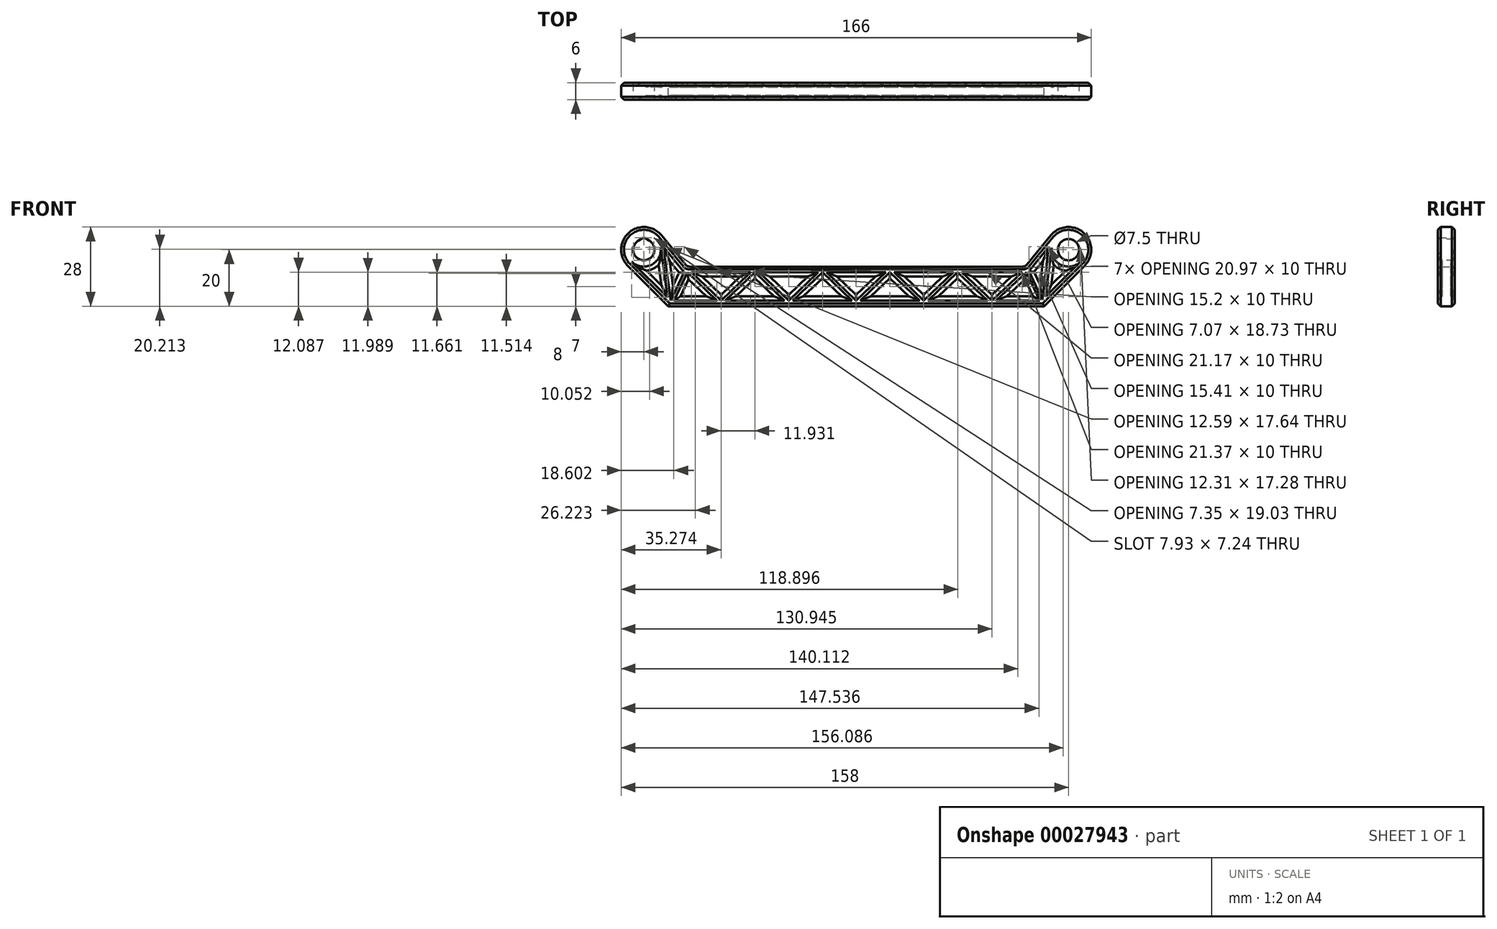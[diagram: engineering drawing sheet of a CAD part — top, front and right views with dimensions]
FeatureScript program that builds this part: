
annotation { "Feature Type Name" : "Feature", "Feature Type Description" : "" }
export const myFeature = defineFeature(function(context is Context, id is Id, definition is map)
    precondition{}
    {
        {
            var Q0;
            Q0=qCreatedBy(makeId("Front.planeOp"),FACE);
            var sketch = newSketch(context, id + "F0", { "sketchPlane" : qUnion([Q0])});
            skArc(sketch, "E0", {"start": v(-68.82, 25.08) * mm, "mid": v(-80.38, 25.92) * mm, "end": v(-80.66, 14.34) * mm});
            skArc(sketch, "E1", {"start": v(80.66, 14.34) * mm, "mid": v(80.38, 25.92) * mm, "end": v(68.82, 25.08) * mm});
            skLineSegment(sketch, "E2", {"start": v(-80.66, 14.34) * mm, "end": v(-66.31, 0) * mm});
            skLineSegment(sketch, "E3", {"start": v(66.31, 0) * mm, "end": v(80.66, 14.34) * mm});
            skLineSegment(sketch, "E4", {"start": v(68.82, 25.08) * mm, "end": v(59.7, 14) * mm});
            skLineSegment(sketch, "E5", {"start": v(59.7, 14) * mm, "end": v(-59.7, 14) * mm});
            skLineSegment(sketch, "E6", {"start": v(-68.82, 25.08) * mm, "end": v(-59.7, 14) * mm});
            skLineSegment(sketch, "E7", {"start": v(-66.31, 0) * mm, "end": v(66.31, 0) * mm});
            skLineSegment(sketch, "E8", {"start": v(59.7, 14) * mm, "end": v(59.7, 0) * mm, "construction": true});
            skLineSegment(sketch, "E9", {"start": v(66.31, 0) * mm, "end": v(55.5, 8.9) * mm, "construction": true});
            skSolve(sketch);
        }
        {
            var Q0;
            Q0 = qSketchRegion(id + "F0", true);
            extrude(context, id + "F1", {"entities" : qUnion([Q0]), "endBound" : BoundingType.SYMMETRIC, "depth" : 6 * mm});
        }
        {
            var Q0;
            Q0=makeQuery(id+"F1.opExtrude","CAP_FACE",FACE,{"disambiguationData":[OSD([sQuery(id+"F0.wireOp",EDGE,"E0"),sQuery(id+"F0.wireOp",EDGE,"E1"),sQuery(id+"F0.wireOp",EDGE,"E2"),sQuery(id+"F0.wireOp",EDGE,"E3"),sQuery(id+"F0.wireOp",EDGE,"E4"),sQuery(id+"F0.wireOp",EDGE,"E5"),sQuery(id+"F0.wireOp",EDGE,"E6"),sQuery(id+"F0.wireOp",EDGE,"E7")])],"isStart":false});
            var sketch = newSketch(context, id + "F2", { "sketchPlane" : qUnion([Q0])});
            skLineSegment(sketch, "E10", {"start": v(-10.48, 12) * mm, "end": v(10.48, 12) * mm});
            skLineSegment(sketch, "E11", {"start": v(10.48, 12) * mm, "end": v(0, 2) * mm});
            skLineSegment(sketch, "E12", {"start": v(0, 2) * mm, "end": v(-10.48, 12) * mm});
            skLineSegment(sketch, "E13", {"start": v(-1.45, 2) * mm, "end": v(-11.93, 12) * mm});
            skLineSegment(sketch, "E14", {"start": v(-11.93, 12) * mm, "end": v(-22.41, 2) * mm});
            skLineSegment(sketch, "E15", {"start": v(-22.41, 2) * mm, "end": v(-1.45, 2) * mm});
            skLineSegment(sketch, "E16", {"start": v(1.45, 2) * mm, "end": v(11.93, 12) * mm});
            skLineSegment(sketch, "E17", {"start": v(11.93, 12) * mm, "end": v(22.41, 2) * mm});
            skLineSegment(sketch, "E18", {"start": v(22.41, 2) * mm, "end": v(1.45, 2) * mm});
            skLineSegment(sketch, "E19", {"start": v(13.38, 12) * mm, "end": v(23.86, 2) * mm});
            skLineSegment(sketch, "E20", {"start": v(13.38, 12) * mm, "end": v(34.35, 12) * mm});
            skLineSegment(sketch, "E21", {"start": v(34.35, 12) * mm, "end": v(23.86, 2) * mm});
            skLineSegment(sketch, "E22", {"start": v(-13.38, 12) * mm, "end": v(-23.86, 2) * mm});
            skLineSegment(sketch, "E23", {"start": v(-23.86, 2) * mm, "end": v(-34.35, 12) * mm});
            skLineSegment(sketch, "E24", {"start": v(-34.35, 12) * mm, "end": v(-13.38, 12) * mm});
            skLineSegment(sketch, "E25", {"start": v(49.4, 2) * mm, "end": v(60.1, 12) * mm});
            skLineSegment(sketch, "E26", {"start": v(60.1, 12) * mm, "end": v(64.82, 2) * mm});
            skLineSegment(sketch, "E27", {"start": v(64.82, 2) * mm, "end": v(49.4, 2) * mm});
            skLineSegment(sketch, "E28", {"start": v(-49.17, 2) * mm, "end": v(-59.66, 12) * mm});
            skLineSegment(sketch, "E29", {"start": v(-59.66, 12) * mm, "end": v(-64.38, 2) * mm});
            skLineSegment(sketch, "E30", {"start": v(-64.38, 2) * mm, "end": v(-49.17, 2) * mm});
            skLineSegment(sketch, "E31", {"start": v(59.7, 14) * mm, "end": v(66.31, 0) * mm, "construction": true});
            skLineSegment(sketch, "E32", {"start": v(-60.72, 12.09) * mm, "end": v(-65.49, 2) * mm});
            skLineSegment(sketch, "E33", {"start": v(-66.65, 3.17) * mm, "end": v(-79.24, 15.76) * mm});
            skLineSegment(sketch, "E34", {"start": v(-68.08, 21.03) * mm, "end": v(-60.72, 12.09) * mm});
            skArc(sketch, "E35", {"start": v(-79.24, 15.76) * mm, "mid": v(-72.33, 14.62) * mm, "end": v(-69.05, 20.8) * mm});
            skLineSegment(sketch, "E36", {"start": v(61, 12.43) * mm, "end": v(65.78, 2.3) * mm});
            skLineSegment(sketch, "E37", {"start": v(66.93, 3.44) * mm, "end": v(79.24, 15.76) * mm});
            skLineSegment(sketch, "E38", {"start": v(-25.31, 2) * mm, "end": v(-46.28, 2) * mm});
            skLineSegment(sketch, "E39", {"start": v(-46.28, 2) * mm, "end": v(-35.8, 12) * mm});
            skLineSegment(sketch, "E40", {"start": v(-35.8, 12) * mm, "end": v(-25.31, 2) * mm});
            skLineSegment(sketch, "E41", {"start": v(-37.24, 12) * mm, "end": v(-58.2, 12) * mm});
            skLineSegment(sketch, "E42", {"start": v(-58.2, 12) * mm, "end": v(-47.73, 2) * mm});
            skLineSegment(sketch, "E43", {"start": v(-47.73, 2) * mm, "end": v(-37.24, 12) * mm});
            skLineSegment(sketch, "E44", {"start": v(35.8, 12) * mm, "end": v(25.31, 2) * mm});
            skLineSegment(sketch, "E45", {"start": v(25.31, 2) * mm, "end": v(46.48, 2) * mm});
            skLineSegment(sketch, "E46", {"start": v(46.48, 2) * mm, "end": v(35.8, 12) * mm});
            skLineSegment(sketch, "E47", {"start": v(58.63, 12) * mm, "end": v(37.26, 12) * mm});
            skLineSegment(sketch, "E48", {"start": v(37.26, 12) * mm, "end": v(47.94, 2) * mm});
            skLineSegment(sketch, "E49", {"start": v(47.94, 2) * mm, "end": v(58.63, 12) * mm});
            skLineSegment(sketch, "E50", {"start": v(-65.49, 2) * mm, "end": v(-68.08, 21.03) * mm});
            skLineSegment(sketch, "E51", {"start": v(-66.65, 3.17) * mm, "end": v(-69.05, 20.8) * mm});
            skLineSegment(sketch, "E52", {"start": v(65.78, 2.3) * mm, "end": v(68.07, 21.02) * mm});
            skLineSegment(sketch, "E53", {"start": v(69.04, 20.73) * mm, "end": v(66.93, 3.44) * mm});
            skLineSegment(sketch, "E54.trimOffspring", {"start": v(68.07, 21.02) * mm, "end": v(61, 12.43) * mm});
            skArc(sketch, "E55.trimOffspring", {"start": v(69.04, 20.73) * mm, "mid": v(72.37, 14.6) * mm, "end": v(79.24, 15.76) * mm});
            skSolve(sketch);
        }
        {
            var Q0;
            Q0 = qSketchRegion(id + "F2", true);
            extrude(context, id + "F3", {"entities" : qUnion([Q0]), "operationType" : NewBodyOperationType.REMOVE, "oppositeDirection" : true, "depth" : 1.5 * mm});
        }
        {
            var Q0;
            Q0=makeQuery(id+"F1.opExtrude","CAP_FACE",FACE,{"disambiguationData":[OSD([sQuery(id+"F0.wireOp",EDGE,"E0"),sQuery(id+"F0.wireOp",EDGE,"E1"),sQuery(id+"F0.wireOp",EDGE,"E2"),sQuery(id+"F0.wireOp",EDGE,"E3"),sQuery(id+"F0.wireOp",EDGE,"E4"),sQuery(id+"F0.wireOp",EDGE,"E5"),sQuery(id+"F0.wireOp",EDGE,"E6"),sQuery(id+"F0.wireOp",EDGE,"E7")])],"isStart":true});
            var sketch = newSketch(context, id + "F4", { "sketchPlane" : qUnion([Q0])});
            skLineSegment(sketch, "E56.0.0", {"start": v(79.24, 15.76) * mm, "end": v(66.65, 3.17) * mm});
            skLineSegment(sketch, "E56.0.1", {"start": v(66.65, 3.17) * mm, "end": v(69.05, 20.8) * mm});
            skArc(sketch, "E56.0.2", {"start": v(69.05, 20.8) * mm, "mid": v(72.33, 14.62) * mm, "end": v(79.24, 15.76) * mm});
            skLineSegment(sketch, "E57.0.0", {"start": v(65.49, 2) * mm, "end": v(60.72, 12.09) * mm});
            skLineSegment(sketch, "E57.0.1", {"start": v(60.72, 12.09) * mm, "end": v(68.08, 21.03) * mm});
            skLineSegment(sketch, "E57.0.2", {"start": v(68.08, 21.03) * mm, "end": v(65.49, 2) * mm});
            skLineSegment(sketch, "E58.0.0", {"start": v(64.38, 2) * mm, "end": v(49.17, 2) * mm});
            skLineSegment(sketch, "E58.0.1", {"start": v(49.17, 2) * mm, "end": v(59.66, 12) * mm});
            skLineSegment(sketch, "E58.0.2", {"start": v(59.66, 12) * mm, "end": v(64.38, 2) * mm});
            skLineSegment(sketch, "E59.0.0", {"start": v(47.73, 2) * mm, "end": v(37.24, 12) * mm});
            skLineSegment(sketch, "E59.0.1", {"start": v(37.24, 12) * mm, "end": v(58.2, 12) * mm});
            skLineSegment(sketch, "E59.0.2", {"start": v(58.2, 12) * mm, "end": v(47.73, 2) * mm});
            skLineSegment(sketch, "E60.0.0", {"start": v(46.28, 2) * mm, "end": v(25.31, 2) * mm});
            skLineSegment(sketch, "E60.0.1", {"start": v(25.31, 2) * mm, "end": v(35.8, 12) * mm});
            skLineSegment(sketch, "E60.0.2", {"start": v(35.8, 12) * mm, "end": v(46.28, 2) * mm});
            skLineSegment(sketch, "E61.0.0", {"start": v(23.86, 2) * mm, "end": v(13.38, 12) * mm});
            skLineSegment(sketch, "E61.0.1", {"start": v(13.38, 12) * mm, "end": v(34.35, 12) * mm});
            skLineSegment(sketch, "E61.0.2", {"start": v(34.35, 12) * mm, "end": v(23.86, 2) * mm});
            skLineSegment(sketch, "E62.0.0", {"start": v(22.41, 2) * mm, "end": v(1.45, 2) * mm});
            skLineSegment(sketch, "E62.0.1", {"start": v(1.45, 2) * mm, "end": v(11.93, 12) * mm});
            skLineSegment(sketch, "E62.0.2", {"start": v(11.93, 12) * mm, "end": v(22.41, 2) * mm});
            skLineSegment(sketch, "E63.0.0", {"start": v(-10.48, 12) * mm, "end": v(10.48, 12) * mm});
            skLineSegment(sketch, "E63.0.1", {"start": v(10.48, 12) * mm, "end": v(0, 2) * mm});
            skLineSegment(sketch, "E63.0.2", {"start": v(0, 2) * mm, "end": v(-10.48, 12) * mm});
            skLineSegment(sketch, "E64.0.0", {"start": v(-11.93, 12) * mm, "end": v(-1.45, 2) * mm});
            skLineSegment(sketch, "E64.0.1", {"start": v(-1.45, 2) * mm, "end": v(-22.41, 2) * mm});
            skLineSegment(sketch, "E64.0.2", {"start": v(-22.41, 2) * mm, "end": v(-11.93, 12) * mm});
            skLineSegment(sketch, "E65.0.0", {"start": v(-34.35, 12) * mm, "end": v(-13.38, 12) * mm});
            skLineSegment(sketch, "E65.0.1", {"start": v(-13.38, 12) * mm, "end": v(-23.86, 2) * mm});
            skLineSegment(sketch, "E65.0.2", {"start": v(-23.86, 2) * mm, "end": v(-34.35, 12) * mm});
            skLineSegment(sketch, "E66.0.0", {"start": v(-46.48, 2) * mm, "end": v(-35.8, 12) * mm});
            skLineSegment(sketch, "E66.0.1", {"start": v(-35.8, 12) * mm, "end": v(-25.31, 2) * mm});
            skLineSegment(sketch, "E66.0.2", {"start": v(-25.31, 2) * mm, "end": v(-46.48, 2) * mm});
            skLineSegment(sketch, "E67.0.0", {"start": v(-47.94, 2) * mm, "end": v(-58.63, 12) * mm});
            skLineSegment(sketch, "E67.0.1", {"start": v(-58.63, 12) * mm, "end": v(-37.26, 12) * mm});
            skLineSegment(sketch, "E67.0.2", {"start": v(-37.26, 12) * mm, "end": v(-47.94, 2) * mm});
            skLineSegment(sketch, "E68.0.0", {"start": v(-60.1, 12) * mm, "end": v(-49.4, 2) * mm});
            skLineSegment(sketch, "E68.0.1", {"start": v(-49.4, 2) * mm, "end": v(-64.82, 2) * mm});
            skLineSegment(sketch, "E68.0.2", {"start": v(-64.82, 2) * mm, "end": v(-60.1, 12) * mm});
            skLineSegment(sketch, "E69.0.0", {"start": v(-68.07, 21.02) * mm, "end": v(-61, 12.43) * mm});
            skLineSegment(sketch, "E69.0.1", {"start": v(-61, 12.43) * mm, "end": v(-65.78, 2.3) * mm});
            skLineSegment(sketch, "E69.0.2", {"start": v(-65.78, 2.3) * mm, "end": v(-68.07, 21.02) * mm});
            skLineSegment(sketch, "E70.0.0", {"start": v(-69.04, 20.73) * mm, "end": v(-66.93, 3.44) * mm});
            skLineSegment(sketch, "E70.0.1", {"start": v(-66.93, 3.44) * mm, "end": v(-79.24, 15.76) * mm});
            skArc(sketch, "E70.0.2", {"start": v(-79.24, 15.76) * mm, "mid": v(-72.37, 14.6) * mm, "end": v(-69.04, 20.73) * mm});
            skSolve(sketch);
        }
        {
            var Q0;
            Q0 = qSketchRegion(id + "F4", true);
            extrude(context, id + "F5", {"entities" : qUnion([Q0]), "operationType" : NewBodyOperationType.REMOVE, "oppositeDirection" : true, "depth" : 1.5 * mm});
        }
        {
            var Q0;
            Q0=makeQuery(id+"F1.opExtrude","CAP_FACE",FACE,{"disambiguationData":[OSD([sQuery(id+"F0.wireOp",EDGE,"E0"),sQuery(id+"F0.wireOp",EDGE,"E1"),sQuery(id+"F0.wireOp",EDGE,"E2"),sQuery(id+"F0.wireOp",EDGE,"E3"),sQuery(id+"F0.wireOp",EDGE,"E4"),sQuery(id+"F0.wireOp",EDGE,"E5"),sQuery(id+"F0.wireOp",EDGE,"E6"),sQuery(id+"F0.wireOp",EDGE,"E7")])],"isStart":false});
            var sketch = newSketch(context, id + "F6", { "sketchPlane" : qUnion([Q0])});
            skCircle(sketch, "E71", {"center": v(-75, 20) * mm, "radius": 3.75 * mm});
            skCircle(sketch, "E72", {"center": v(75, 20) * mm, "radius": 3.75 * mm});
            skSolve(sketch);
        }
        {
            var Q0;
            Q0 = qSketchRegion(id + "F6", true);
            extrude(context, id + "F7", {"entities" : qUnion([Q0]), "operationType" : NewBodyOperationType.REMOVE, "endBound" : BoundingType.THROUGH_ALL, "oppositeDirection" : true, "depth" : 25 * mm});
        }
        {
            var Q0;
            Q0=makeQuery(id+"F1.opExtrude","SWEPT_EDGE",EDGE,{"disambiguationData":[OSD([sQuery(id+"F0.wireOp",EDGE,"E5"),sQuery(id+"F0.wireOp",EDGE,"E6")])]});
            var Q1;
            Q1=makeQuery(id+"F1.opExtrude","SWEPT_EDGE",EDGE,{"disambiguationData":[OSD([sQuery(id+"F0.wireOp",EDGE,"E4"),sQuery(id+"F0.wireOp",EDGE,"E5")])]});
            fillet(context, id + "F8", {"entities" : qUnion([Q0, Q1]), "radius" : 2 * mm, "tangentPropagation" : true, "allowEdgeOverflow" : false});
        }
        {
            var Q0;
            Q0=makeQuery(id+"F1.opExtrude","CAP_EDGE",EDGE,{"disambiguationData":[OSD([sQuery(id+"F0.wireOp",EDGE,"E5")])],"isStart":true});
            var Q1;
            Q1=makeQuery(id+"F1.opExtrude","CAP_EDGE",EDGE,{"disambiguationData":[OSD([sQuery(id+"F0.wireOp",EDGE,"E5")])],"isStart":false});
            var Q2;
            Q2=makeQuery(id+"F1.opExtrude","CAP_EDGE",EDGE,{"disambiguationData":[OSD([sQuery(id+"F0.wireOp",EDGE,"E7")])],"isStart":false});
            var Q3;
            Q3=makeQuery(id+"F1.opExtrude","CAP_EDGE",EDGE,{"disambiguationData":[OSD([sQuery(id+"F0.wireOp",EDGE,"E7")])],"isStart":true});
            chamfer(context, id + "F9", {"entities" : qUnion([Q0, Q1, Q2, Q3]), "width" : 1 * mm, "tangentPropagation" : true});
        }
        {
            var Q0;
            Q0=makeQuery(id+"F3.boolean.opBoolean","COPY",FACE,{"derivedFrom":makeQuery(id+"F3.opExtrude","CAP_FACE",FACE,{"disambiguationData":[OSD([sQuery(id+"F2.wireOp",EDGE,"E32"),sQuery(id+"F2.wireOp",EDGE,"E33"),sQuery(id+"F2.wireOp",EDGE,"c86ce3fd-6d6f-4e97-870f-5ae21d41f3c9")])],"isStart":false})});
            var Q1;
            Q1=makeQuery(id+"F3.boolean.opBoolean","COPY",FACE,{"derivedFrom":makeQuery(id+"F3.opExtrude","CAP_FACE",FACE,{"disambiguationData":[OSD([sQuery(id+"F2.wireOp",EDGE,"E28"),sQuery(id+"F2.wireOp",EDGE,"E29"),sQuery(id+"F2.wireOp",EDGE,"E30")])],"isStart":false})});
            var Q2;
            Q2=makeQuery(id+"F3.boolean.opBoolean","COPY",FACE,{"derivedFrom":makeQuery(id+"F3.opExtrude","CAP_FACE",FACE,{"disambiguationData":[OSD([sQuery(id+"F2.wireOp",EDGE,"E41"),sQuery(id+"F2.wireOp",EDGE,"E42"),sQuery(id+"F2.wireOp",EDGE,"E43")])],"isStart":false})});
            var Q3;
            Q3=makeQuery(id+"F3.boolean.opBoolean","COPY",FACE,{"derivedFrom":makeQuery(id+"F3.opExtrude","CAP_FACE",FACE,{"disambiguationData":[OSD([sQuery(id+"F2.wireOp",EDGE,"E38"),sQuery(id+"F2.wireOp",EDGE,"E39"),sQuery(id+"F2.wireOp",EDGE,"E40")])],"isStart":false})});
            var Q4;
            Q4=makeQuery(id+"F3.boolean.opBoolean","COPY",FACE,{"derivedFrom":makeQuery(id+"F3.opExtrude","CAP_FACE",FACE,{"disambiguationData":[OSD([sQuery(id+"F2.wireOp",EDGE,"E22"),sQuery(id+"F2.wireOp",EDGE,"E23"),sQuery(id+"F2.wireOp",EDGE,"E24")])],"isStart":false})});
            var Q5;
            Q5=makeQuery(id+"F3.boolean.opBoolean","COPY",FACE,{"derivedFrom":makeQuery(id+"F3.opExtrude","CAP_FACE",FACE,{"disambiguationData":[OSD([sQuery(id+"F2.wireOp",EDGE,"E13"),sQuery(id+"F2.wireOp",EDGE,"E14"),sQuery(id+"F2.wireOp",EDGE,"E15")])],"isStart":false})});
            var Q6;
            Q6=makeQuery(id+"F3.boolean.opBoolean","COPY",FACE,{"derivedFrom":makeQuery(id+"F3.opExtrude","CAP_FACE",FACE,{"disambiguationData":[OSD([sQuery(id+"F2.wireOp",EDGE,"E10"),sQuery(id+"F2.wireOp",EDGE,"E11"),sQuery(id+"F2.wireOp",EDGE,"E12")])],"isStart":false})});
            var Q7;
            Q7=makeQuery(id+"F3.boolean.opBoolean","COPY",FACE,{"derivedFrom":makeQuery(id+"F3.opExtrude","CAP_FACE",FACE,{"disambiguationData":[OSD([sQuery(id+"F2.wireOp",EDGE,"E16"),sQuery(id+"F2.wireOp",EDGE,"E17"),sQuery(id+"F2.wireOp",EDGE,"E18")])],"isStart":false})});
            var Q8;
            Q8=makeQuery(id+"F3.boolean.opBoolean","COPY",FACE,{"derivedFrom":makeQuery(id+"F3.opExtrude","CAP_FACE",FACE,{"disambiguationData":[OSD([sQuery(id+"F2.wireOp",EDGE,"E19"),sQuery(id+"F2.wireOp",EDGE,"E20"),sQuery(id+"F2.wireOp",EDGE,"E21")])],"isStart":false})});
            var Q9;
            Q9=makeQuery(id+"F3.boolean.opBoolean","COPY",FACE,{"derivedFrom":makeQuery(id+"F3.opExtrude","CAP_FACE",FACE,{"disambiguationData":[OSD([sQuery(id+"F2.wireOp",EDGE,"E44"),sQuery(id+"F2.wireOp",EDGE,"E45"),sQuery(id+"F2.wireOp",EDGE,"E46")])],"isStart":false})});
            var Q10;
            Q10=makeQuery(id+"F3.boolean.opBoolean","COPY",FACE,{"derivedFrom":makeQuery(id+"F3.opExtrude","CAP_FACE",FACE,{"disambiguationData":[OSD([sQuery(id+"F2.wireOp",EDGE,"E47"),sQuery(id+"F2.wireOp",EDGE,"E48"),sQuery(id+"F2.wireOp",EDGE,"E49")])],"isStart":false})});
            var Q11;
            Q11=makeQuery(id+"F3.boolean.opBoolean","COPY",FACE,{"derivedFrom":makeQuery(id+"F3.opExtrude","CAP_FACE",FACE,{"disambiguationData":[OSD([sQuery(id+"F2.wireOp",EDGE,"E36"),sQuery(id+"F2.wireOp",EDGE,"E37"),sQuery(id+"F2.wireOp",EDGE,"b1a802d5-c466-4d59-abdb-8e271099b131")])],"isStart":false})});
            var Q12;
            Q12=makeQuery(id+"F3.boolean.opBoolean","COPY",FACE,{"derivedFrom":makeQuery(id+"F3.opExtrude","CAP_FACE",FACE,{"disambiguationData":[OSD([sQuery(id+"F2.wireOp",EDGE,"E25"),sQuery(id+"F2.wireOp",EDGE,"E26"),sQuery(id+"F2.wireOp",EDGE,"E27")])],"isStart":false})});
            var Q13;
            Q13=makeQuery(id+"F5.boolean.opBoolean","COPY",FACE,{"derivedFrom":makeQuery(id+"F5.opExtrude","CAP_FACE",FACE,{"disambiguationData":[OSD([sQuery(id+"F4.wireOp",EDGE,"c57d27d1-84c8-4695-a057-162f5bee0dce.0.0"),sQuery(id+"F4.wireOp",EDGE,"c57d27d1-84c8-4695-a057-162f5bee0dce.0.1"),sQuery(id+"F4.wireOp",EDGE,"c57d27d1-84c8-4695-a057-162f5bee0dce.0.2")])],"isStart":false})});
            var Q14;
            Q14=makeQuery(id+"F5.boolean.opBoolean","COPY",FACE,{"derivedFrom":makeQuery(id+"F5.opExtrude","CAP_FACE",FACE,{"disambiguationData":[OSD([sQuery(id+"F4.wireOp",EDGE,"5e8aeb78-e5a0-42a7-b254-9315b7273d8a.0.0"),sQuery(id+"F4.wireOp",EDGE,"5e8aeb78-e5a0-42a7-b254-9315b7273d8a.0.1"),sQuery(id+"F4.wireOp",EDGE,"5e8aeb78-e5a0-42a7-b254-9315b7273d8a.0.2")])],"isStart":false})});
            var Q15;
            Q15=makeQuery(id+"F5.boolean.opBoolean","COPY",FACE,{"derivedFrom":makeQuery(id+"F5.opExtrude","CAP_FACE",FACE,{"disambiguationData":[OSD([sQuery(id+"F4.wireOp",EDGE,"1ce46735-0278-4186-8825-73dcd0464fbd.0.0"),sQuery(id+"F4.wireOp",EDGE,"1ce46735-0278-4186-8825-73dcd0464fbd.0.1"),sQuery(id+"F4.wireOp",EDGE,"1ce46735-0278-4186-8825-73dcd0464fbd.0.2")])],"isStart":false})});
            var Q16;
            Q16=makeQuery(id+"F5.boolean.opBoolean","COPY",FACE,{"derivedFrom":makeQuery(id+"F5.opExtrude","CAP_FACE",FACE,{"disambiguationData":[OSD([sQuery(id+"F4.wireOp",EDGE,"382fdfe6-d7b0-4580-a637-7794371c19b0.0.0"),sQuery(id+"F4.wireOp",EDGE,"382fdfe6-d7b0-4580-a637-7794371c19b0.0.1"),sQuery(id+"F4.wireOp",EDGE,"382fdfe6-d7b0-4580-a637-7794371c19b0.0.2")])],"isStart":false})});
            var Q17;
            Q17=makeQuery(id+"F5.boolean.opBoolean","COPY",FACE,{"derivedFrom":makeQuery(id+"F5.opExtrude","CAP_FACE",FACE,{"disambiguationData":[OSD([sQuery(id+"F4.wireOp",EDGE,"62df2a1e-98e2-4660-bf50-3cd35c4cc82d.0.0"),sQuery(id+"F4.wireOp",EDGE,"62df2a1e-98e2-4660-bf50-3cd35c4cc82d.0.1"),sQuery(id+"F4.wireOp",EDGE,"62df2a1e-98e2-4660-bf50-3cd35c4cc82d.0.2")])],"isStart":false})});
            var Q18;
            Q18=makeQuery(id+"F5.boolean.opBoolean","COPY",FACE,{"derivedFrom":makeQuery(id+"F5.opExtrude","CAP_FACE",FACE,{"disambiguationData":[OSD([sQuery(id+"F4.wireOp",EDGE,"f5310118-96e3-44cf-a066-d1ddce517366.0.0"),sQuery(id+"F4.wireOp",EDGE,"f5310118-96e3-44cf-a066-d1ddce517366.0.1"),sQuery(id+"F4.wireOp",EDGE,"f5310118-96e3-44cf-a066-d1ddce517366.0.2")])],"isStart":false})});
            var Q19;
            Q19=makeQuery(id+"F5.boolean.opBoolean","COPY",FACE,{"derivedFrom":makeQuery(id+"F5.opExtrude","CAP_FACE",FACE,{"disambiguationData":[OSD([sQuery(id+"F4.wireOp",EDGE,"4087ecb6-3a4e-4780-933b-568754845fe0.0.0"),sQuery(id+"F4.wireOp",EDGE,"4087ecb6-3a4e-4780-933b-568754845fe0.0.1"),sQuery(id+"F4.wireOp",EDGE,"4087ecb6-3a4e-4780-933b-568754845fe0.0.2")])],"isStart":false})});
            var Q20;
            Q20=makeQuery(id+"F5.boolean.opBoolean","COPY",FACE,{"derivedFrom":makeQuery(id+"F5.opExtrude","CAP_FACE",FACE,{"disambiguationData":[OSD([sQuery(id+"F4.wireOp",EDGE,"821c492d-ad28-4405-b8a1-e58fb1ca5f4b.0.0"),sQuery(id+"F4.wireOp",EDGE,"821c492d-ad28-4405-b8a1-e58fb1ca5f4b.0.1"),sQuery(id+"F4.wireOp",EDGE,"821c492d-ad28-4405-b8a1-e58fb1ca5f4b.0.2")])],"isStart":false})});
            var Q21;
            Q21=makeQuery(id+"F5.boolean.opBoolean","COPY",FACE,{"derivedFrom":makeQuery(id+"F5.opExtrude","CAP_FACE",FACE,{"disambiguationData":[OSD([sQuery(id+"F4.wireOp",EDGE,"31772469-9332-4179-9cb1-8d0c005ea144.0.0"),sQuery(id+"F4.wireOp",EDGE,"31772469-9332-4179-9cb1-8d0c005ea144.0.1"),sQuery(id+"F4.wireOp",EDGE,"31772469-9332-4179-9cb1-8d0c005ea144.0.2")])],"isStart":false})});
            var Q22;
            Q22=makeQuery(id+"F5.boolean.opBoolean","COPY",FACE,{"derivedFrom":makeQuery(id+"F5.opExtrude","CAP_FACE",FACE,{"disambiguationData":[OSD([sQuery(id+"F4.wireOp",EDGE,"f02140a4-729b-451f-9ad4-0e91208db16a.0.0"),sQuery(id+"F4.wireOp",EDGE,"f02140a4-729b-451f-9ad4-0e91208db16a.0.1"),sQuery(id+"F4.wireOp",EDGE,"f02140a4-729b-451f-9ad4-0e91208db16a.0.2")])],"isStart":false})});
            var Q23;
            Q23=makeQuery(id+"F5.boolean.opBoolean","COPY",FACE,{"derivedFrom":makeQuery(id+"F5.opExtrude","CAP_FACE",FACE,{"disambiguationData":[OSD([sQuery(id+"F4.wireOp",EDGE,"0ff050ed-1b77-4dcf-8ca6-53e2329c6a8a.0.0"),sQuery(id+"F4.wireOp",EDGE,"0ff050ed-1b77-4dcf-8ca6-53e2329c6a8a.0.1"),sQuery(id+"F4.wireOp",EDGE,"0ff050ed-1b77-4dcf-8ca6-53e2329c6a8a.0.2")])],"isStart":false})});
            var Q24;
            Q24=makeQuery(id+"F5.boolean.opBoolean","COPY",FACE,{"derivedFrom":makeQuery(id+"F5.opExtrude","CAP_FACE",FACE,{"disambiguationData":[OSD([sQuery(id+"F4.wireOp",EDGE,"17b64185-96cc-4730-8b5c-38b3cf217d73.0.0"),sQuery(id+"F4.wireOp",EDGE,"17b64185-96cc-4730-8b5c-38b3cf217d73.0.1"),sQuery(id+"F4.wireOp",EDGE,"17b64185-96cc-4730-8b5c-38b3cf217d73.0.2")])],"isStart":false})});
            var Q25;
            Q25=makeQuery(id+"F5.boolean.opBoolean","COPY",FACE,{"derivedFrom":makeQuery(id+"F5.opExtrude","CAP_FACE",FACE,{"disambiguationData":[OSD([sQuery(id+"F4.wireOp",EDGE,"a12985bd-35d4-486b-a94e-5bbb5bad177a.0.0"),sQuery(id+"F4.wireOp",EDGE,"a12985bd-35d4-486b-a94e-5bbb5bad177a.0.1"),sQuery(id+"F4.wireOp",EDGE,"a12985bd-35d4-486b-a94e-5bbb5bad177a.0.2")])],"isStart":false})});
            var Q26;
            Q26=makeQuery(id+"F5.boolean.opBoolean","COPY",FACE,{"derivedFrom":makeQuery(id+"F5.opExtrude","CAP_FACE",FACE,{"disambiguationData":[OSD([sQuery(id+"F4.wireOp",EDGE,"E70.0.0"),sQuery(id+"F4.wireOp",EDGE,"E70.0.1"),sQuery(id+"F4.wireOp",EDGE,"E70.0.2")])],"isStart":false})});
            var Q27;
            Q27=makeQuery(id+"F5.boolean.opBoolean","COPY",FACE,{"derivedFrom":makeQuery(id+"F5.opExtrude","CAP_FACE",FACE,{"disambiguationData":[OSD([sQuery(id+"F4.wireOp",EDGE,"E69.0.0"),sQuery(id+"F4.wireOp",EDGE,"E69.0.1"),sQuery(id+"F4.wireOp",EDGE,"E69.0.2")])],"isStart":false})});
            var Q28;
            Q28=makeQuery(id+"F5.boolean.opBoolean","COPY",FACE,{"derivedFrom":makeQuery(id+"F5.opExtrude","CAP_FACE",FACE,{"disambiguationData":[OSD([sQuery(id+"F4.wireOp",EDGE,"E68.0.0"),sQuery(id+"F4.wireOp",EDGE,"E68.0.1"),sQuery(id+"F4.wireOp",EDGE,"E68.0.2")])],"isStart":false})});
            var Q29;
            Q29=makeQuery(id+"F5.boolean.opBoolean","COPY",FACE,{"derivedFrom":makeQuery(id+"F5.opExtrude","CAP_FACE",FACE,{"disambiguationData":[OSD([sQuery(id+"F4.wireOp",EDGE,"E67.0.0"),sQuery(id+"F4.wireOp",EDGE,"E67.0.1"),sQuery(id+"F4.wireOp",EDGE,"E67.0.2")])],"isStart":false})});
            var Q30;
            Q30=makeQuery(id+"F5.boolean.opBoolean","COPY",FACE,{"derivedFrom":makeQuery(id+"F5.opExtrude","CAP_FACE",FACE,{"disambiguationData":[OSD([sQuery(id+"F4.wireOp",EDGE,"E66.0.0"),sQuery(id+"F4.wireOp",EDGE,"E66.0.1"),sQuery(id+"F4.wireOp",EDGE,"E66.0.2")])],"isStart":false})});
            var Q31;
            Q31=makeQuery(id+"F5.boolean.opBoolean","COPY",FACE,{"derivedFrom":makeQuery(id+"F5.opExtrude","CAP_FACE",FACE,{"disambiguationData":[OSD([sQuery(id+"F4.wireOp",EDGE,"E65.0.0"),sQuery(id+"F4.wireOp",EDGE,"E65.0.1"),sQuery(id+"F4.wireOp",EDGE,"E65.0.2")])],"isStart":false})});
            var Q32;
            Q32=makeQuery(id+"F5.boolean.opBoolean","COPY",FACE,{"derivedFrom":makeQuery(id+"F5.opExtrude","CAP_FACE",FACE,{"disambiguationData":[OSD([sQuery(id+"F4.wireOp",EDGE,"E64.0.0"),sQuery(id+"F4.wireOp",EDGE,"E64.0.1"),sQuery(id+"F4.wireOp",EDGE,"E64.0.2")])],"isStart":false})});
            var Q33;
            Q33=makeQuery(id+"F5.boolean.opBoolean","COPY",FACE,{"derivedFrom":makeQuery(id+"F5.opExtrude","CAP_FACE",FACE,{"disambiguationData":[OSD([sQuery(id+"F4.wireOp",EDGE,"E63.0.0"),sQuery(id+"F4.wireOp",EDGE,"E63.0.1"),sQuery(id+"F4.wireOp",EDGE,"E63.0.2")])],"isStart":false})});
            var Q34;
            Q34=makeQuery(id+"F5.boolean.opBoolean","COPY",FACE,{"derivedFrom":makeQuery(id+"F5.opExtrude","CAP_FACE",FACE,{"disambiguationData":[OSD([sQuery(id+"F4.wireOp",EDGE,"E62.0.0"),sQuery(id+"F4.wireOp",EDGE,"E62.0.1"),sQuery(id+"F4.wireOp",EDGE,"E62.0.2")])],"isStart":false})});
            var Q35;
            Q35=makeQuery(id+"F5.boolean.opBoolean","COPY",FACE,{"derivedFrom":makeQuery(id+"F5.opExtrude","CAP_FACE",FACE,{"disambiguationData":[OSD([sQuery(id+"F4.wireOp",EDGE,"E61.0.0"),sQuery(id+"F4.wireOp",EDGE,"E61.0.1"),sQuery(id+"F4.wireOp",EDGE,"E61.0.2")])],"isStart":false})});
            var Q36;
            Q36=makeQuery(id+"F5.boolean.opBoolean","COPY",FACE,{"derivedFrom":makeQuery(id+"F5.opExtrude","CAP_FACE",FACE,{"disambiguationData":[OSD([sQuery(id+"F4.wireOp",EDGE,"E60.0.0"),sQuery(id+"F4.wireOp",EDGE,"E60.0.1"),sQuery(id+"F4.wireOp",EDGE,"E60.0.2")])],"isStart":false})});
            var Q37;
            Q37=makeQuery(id+"F5.boolean.opBoolean","COPY",FACE,{"derivedFrom":makeQuery(id+"F5.opExtrude","CAP_FACE",FACE,{"disambiguationData":[OSD([sQuery(id+"F4.wireOp",EDGE,"E59.0.0"),sQuery(id+"F4.wireOp",EDGE,"E59.0.1"),sQuery(id+"F4.wireOp",EDGE,"E59.0.2")])],"isStart":false})});
            var Q38;
            Q38=makeQuery(id+"F5.boolean.opBoolean","COPY",FACE,{"derivedFrom":makeQuery(id+"F5.opExtrude","CAP_FACE",FACE,{"disambiguationData":[OSD([sQuery(id+"F4.wireOp",EDGE,"E58.0.0"),sQuery(id+"F4.wireOp",EDGE,"E58.0.1"),sQuery(id+"F4.wireOp",EDGE,"E58.0.2")])],"isStart":false})});
            var Q39;
            Q39=makeQuery(id+"F5.boolean.opBoolean","COPY",FACE,{"derivedFrom":makeQuery(id+"F5.opExtrude","CAP_FACE",FACE,{"disambiguationData":[OSD([sQuery(id+"F4.wireOp",EDGE,"E57.0.0"),sQuery(id+"F4.wireOp",EDGE,"E57.0.1"),sQuery(id+"F4.wireOp",EDGE,"E57.0.2")])],"isStart":false})});
            var Q40;
            Q40=makeQuery(id+"F5.boolean.opBoolean","COPY",FACE,{"derivedFrom":makeQuery(id+"F5.opExtrude","CAP_FACE",FACE,{"disambiguationData":[OSD([sQuery(id+"F4.wireOp",EDGE,"E56.0.0"),sQuery(id+"F4.wireOp",EDGE,"E56.0.1"),sQuery(id+"F4.wireOp",EDGE,"E56.0.2")])],"isStart":false})});
            chamfer(context, id + "F10", {"entities" : qUnion([Q0, Q1, Q2, Q3, Q4, Q5, Q6, Q7, Q8, Q9, Q10, Q11, Q12, Q13, Q14, Q15, Q16, Q17, Q18, Q19, Q20, Q21, Q22, Q23, Q24, Q25, Q26, Q27, Q28, Q29, Q30, Q31, Q32, Q33, Q34, Q35, Q36, Q37, Q38, Q39, Q40]), "width" : 1.5 * mm, "tangentPropagation" : true});
        }
        {
            var Q0;
            Q0=makeQuery(id+"F1.opExtrude","CAP_FACE",FACE,{"disambiguationData":[OSD([sQuery(id+"F0.wireOp",EDGE,"E0"),sQuery(id+"F0.wireOp",EDGE,"E1"),sQuery(id+"F0.wireOp",EDGE,"E2"),sQuery(id+"F0.wireOp",EDGE,"E3"),sQuery(id+"F0.wireOp",EDGE,"E4"),sQuery(id+"F0.wireOp",EDGE,"E5"),sQuery(id+"F0.wireOp",EDGE,"E6"),sQuery(id+"F0.wireOp",EDGE,"E7")])],"isStart":false});
            var sketch = newSketch(context, id + "F11", { "sketchPlane" : qUnion([Q0])});
            skLineSegment(sketch, "E73", {"start": v(-76.88, 23.25) * mm, "end": v(-75, 24.33) * mm});
            skLineSegment(sketch, "E74", {"start": v(-75, 24.33) * mm, "end": v(-73.12, 23.25) * mm});
            skLineSegment(sketch, "E75", {"start": v(-73.12, 23.25) * mm, "end": v(-76.88, 23.25) * mm});
            skSolve(sketch);
        }
        {
            var Q0;
            Q0 = qSketchRegion(id + "F11", true);
            extrude(context, id + "F12", {"entities" : qUnion([Q0]), "operationType" : NewBodyOperationType.REMOVE, "endBound" : BoundingType.THROUGH_ALL, "oppositeDirection" : true, "depth" : 25 * mm});
        }
        {
            var Q0;
            Q0=makeQuery(id+"F12.boolean.opBoolean","COPY",EDGE,{"derivedFrom":makeQuery(id+"F12.opExtrude","SWEPT_EDGE",EDGE,{"disambiguationData":[OSD([sQuery(id+"F11.wireOp",EDGE,"E73"),sQuery(id+"F11.wireOp",EDGE,"E74")])]})});
            fillet(context, id + "F13", {"entities" : qUnion([Q0]), "radius" : 1 * mm, "tangentPropagation" : true, "allowEdgeOverflow" : false});
        }
    });
